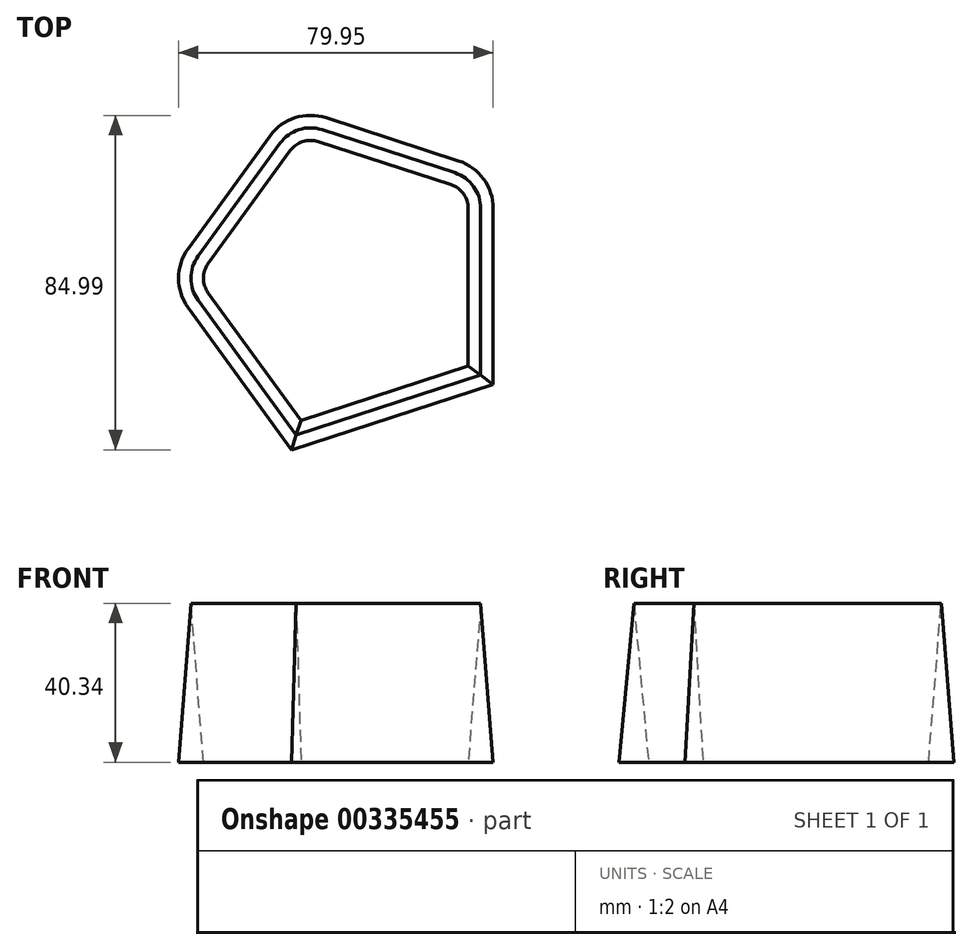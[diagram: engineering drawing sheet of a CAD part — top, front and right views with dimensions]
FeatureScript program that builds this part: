
annotation { "Feature Type Name" : "Feature", "Feature Type Description" : "" }
export const myFeature = defineFeature(function(context is Context, id is Id, definition is map)
    precondition{}
    {
        {
            var Q0;
            Q0=qCreatedBy(makeId("Top.planeOp"),FACE);
            var sketch = newSketch(context, id + "F0", { "sketchPlane" : qUnion([Q0])});
            skCircle(sketch, "E0.cCircle", {"center": v(0, 0) * mm, "radius": 37.1 * mm, "construction": true});
            skLineSegment(sketch, "E0.0", {"start": v(37.1, 17.72) * mm, "end": v(37.1, -26.95) * mm});
            skLineSegment(sketch, "E0.1", {"start": v(37.1, -26.95) * mm, "end": v(-14.17, -43.6) * mm});
            skLineSegment(sketch, "E0.2", {"start": v(-14.17, -43.6) * mm, "end": v(-40.43, -7.46) * mm});
            skLineSegment(sketch, "E0.3", {"start": v(-40.43, 7.46) * mm, "end": v(-19.6, 36.14) * mm});
            skLineSegment(sketch, "E0.4", {"start": v(-5.4, 40.76) * mm, "end": v(28.32, 29.8) * mm});
            skPoint(sketch, "E0.0.midPoint", {"position": v(37.1, 0) * mm});
            skPoint(sketch, "E1.visualSharp", {"position": v(-14.17, 43.6) * mm});
            skArc(sketch, "E1.filletArc", {"start": v(-5.4, 40.76) * mm, "mid": v(-13.24, 40.76) * mm, "end": v(-19.6, 36.14) * mm});
            skPoint(sketch, "E2.visualSharp", {"position": v(-45.85, 0) * mm});
            skArc(sketch, "E2.filletArc", {"start": v(-40.43, 7.46) * mm, "mid": v(-42.85, 0) * mm, "end": v(-40.43, -7.46) * mm});
            skPoint(sketch, "E3.visualSharp", {"position": v(37.1, 26.95) * mm});
            skArc(sketch, "E3.filletArc", {"start": v(37.1, 17.72) * mm, "mid": v(34.67, 25.19) * mm, "end": v(28.32, 29.8) * mm});
            skLineSegment(sketch, "E4.0", {"start": v(-35.3, 3.73) * mm, "end": v(-14.46, 32.41) * mm});
            skArc(sketch, "E4.1", {"start": v(-7.36, 34.72) * mm, "mid": v(-11.28, 34.72) * mm, "end": v(-14.46, 32.41) * mm});
            skArc(sketch, "E4.2", {"start": v(-35.3, 3.73) * mm, "mid": v(-36.5, 0) * mm, "end": v(-35.3, -3.73) * mm});
            skLineSegment(sketch, "E4.3", {"start": v(-7.36, 34.72) * mm, "end": v(26.36, 23.76) * mm});
            skLineSegment(sketch, "E4.4", {"start": v(-11.74, -36.14) * mm, "end": v(-35.3, -3.73) * mm});
            skLineSegment(sketch, "E4.5", {"start": v(30.75, -22.34) * mm, "end": v(-11.74, -36.14) * mm});
            skLineSegment(sketch, "E4.6", {"start": v(30.75, 17.72) * mm, "end": v(30.75, -22.34) * mm});
            skArc(sketch, "E4.7", {"start": v(30.75, 17.72) * mm, "mid": v(29.53, 21.46) * mm, "end": v(26.36, 23.76) * mm});
            skSolve(sketch);
        }
        {
            var Q0;
            Q0 = qSketchRegion(id + "F0", true);
            extrude(context, id + "F1", {"entities" : qUnion([Q0]), "depth" : 85.34 * mm, "hasDraft" : true, "draftAngle" : 4.5 * degree, "draftPullDirection" : true});
        }
    });
